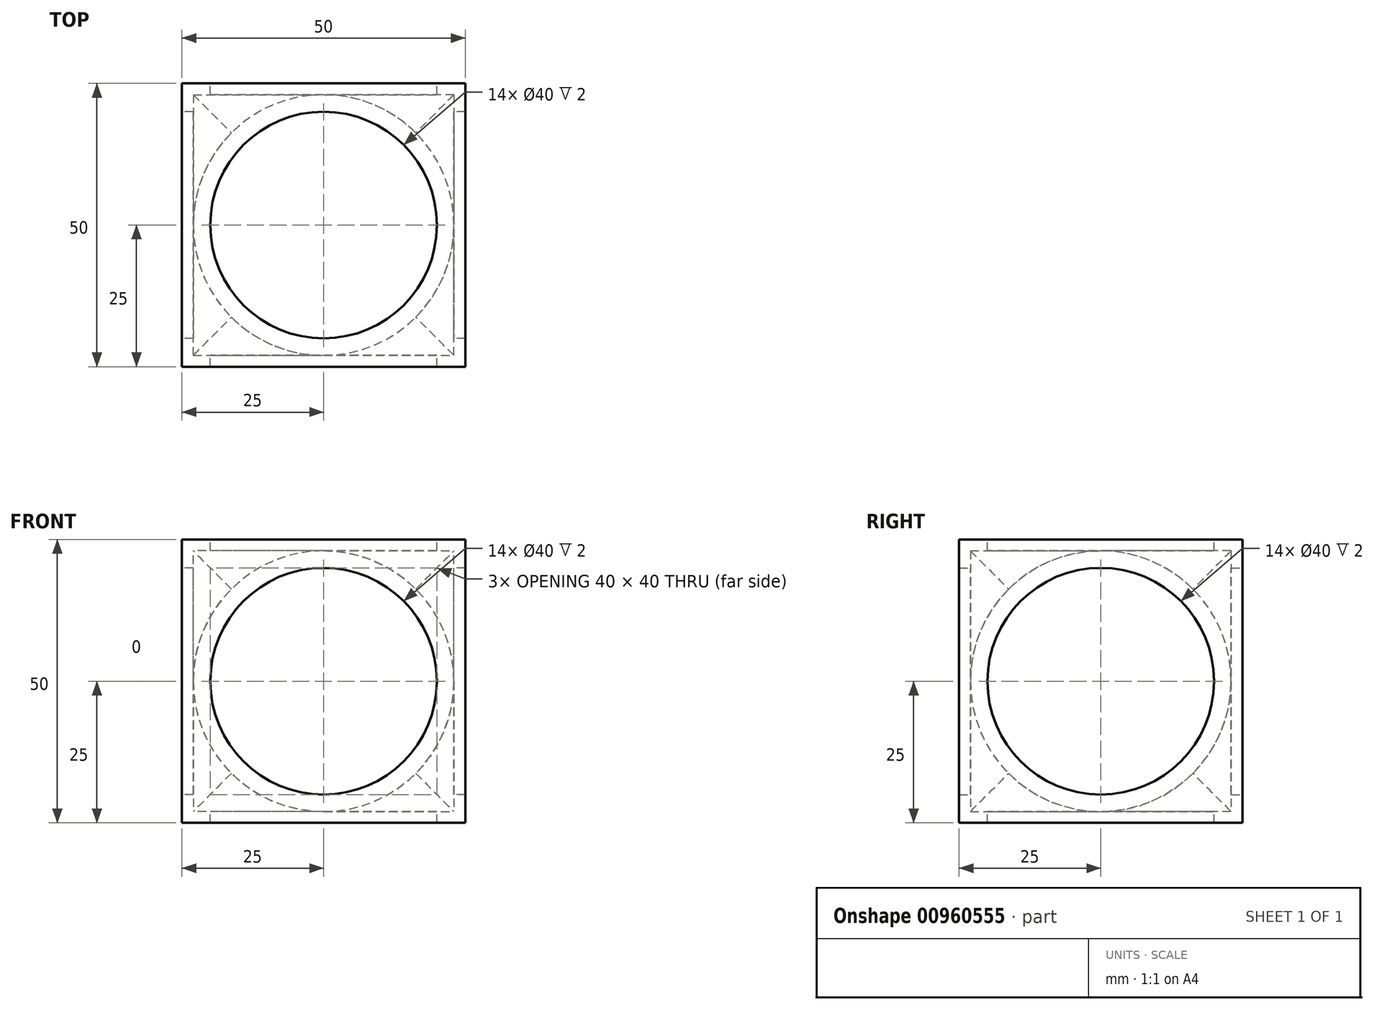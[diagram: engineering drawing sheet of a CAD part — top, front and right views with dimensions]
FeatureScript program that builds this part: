
annotation { "Feature Type Name" : "Feature", "Feature Type Description" : "" }
export const myFeature = defineFeature(function(context is Context, id is Id, definition is map)
    precondition{}
    {
        {
            var Q0;
            Q0=qCreatedBy(makeId("Top.planeOp"),FACE);
            var sketch = newSketch(context, id + "F0", { "sketchPlane" : qUnion([Q0])});
            skLineSegment(sketch, "E0.bottom", {"start": v(25, 25) * mm, "end": v(-25, 25) * mm});
            skLineSegment(sketch, "E0.top", {"start": v(25, -25) * mm, "end": v(-25, -25) * mm});
            skLineSegment(sketch, "E0.left", {"start": v(25, 25) * mm, "end": v(25, -25) * mm});
            skLineSegment(sketch, "E0.right", {"start": v(-25, 25) * mm, "end": v(-25, -25) * mm});
            skPoint(sketch, "E0.middle", {"position": v(0, 0) * mm});
            skSolve(sketch);
        }
        {
            var Q0;
            Q0 = qSketchRegion(id + "F0", true);
            extrude(context, id + "F1", {"entities" : qUnion([Q0]), "endBound" : BoundingType.SYMMETRIC, "depth" : 50 * mm, "offsetDistance" : 25 * mm});
        }
        {
            var Q0;
            Q0=makeQuery(id+"F1.opExtrude","CAP_FACE",FACE,{"disambiguationData":[OSD([sQuery(id+"F0.wireOp",EDGE,"E0.bottom"),sQuery(id+"F0.wireOp",EDGE,"E0.top"),sQuery(id+"F0.wireOp",EDGE,"E0.left"),sQuery(id+"F0.wireOp",EDGE,"E0.right")])],"isStart":false});
            var sketch = newSketch(context, id + "F2", { "sketchPlane" : qUnion([Q0])});
            skCircle(sketch, "E1", {"center": v(0, 0) * mm, "radius": 20 * mm});
            skSolve(sketch);
        }
        {
            var Q0;
            Q0 = qSketchRegion(id + "F2", true);
            extrude(context, id + "F3", {"entities" : qUnion([Q0]), "operationType" : NewBodyOperationType.REMOVE, "endBound" : BoundingType.THROUGH_ALL, "oppositeDirection" : true, "depth" : 25 * mm, "offsetDistance" : 25 * mm});
        }
        {
            var Q0;
            Q0=makeQuery(id+"F1.opExtrude","SWEPT_FACE",FACE,{"disambiguationData":[OSD([sQuery(id+"F0.wireOp",EDGE,"E0.bottom")])]});
            var sketch = newSketch(context, id + "F4", { "sketchPlane" : qUnion([Q0])});
            skCircle(sketch, "E2", {"center": v(0, 0) * mm, "radius": 20 * mm});
            skSolve(sketch);
        }
        {
            var Q0;
            Q0 = qSketchRegion(id + "F4", true);
            extrude(context, id + "F5", {"entities" : qUnion([Q0]), "operationType" : NewBodyOperationType.REMOVE, "endBound" : BoundingType.THROUGH_ALL, "oppositeDirection" : true, "depth" : 25 * mm, "offsetDistance" : 25 * mm});
        }
        {
            var Q0;
            Q0=makeQuery(id+"F1.opExtrude","SWEPT_FACE",FACE,{"disambiguationData":[OSD([sQuery(id+"F0.wireOp",EDGE,"E0.right")])]});
            var sketch = newSketch(context, id + "F6", { "sketchPlane" : qUnion([Q0])});
            skCircle(sketch, "E3", {"center": v(0, 0) * mm, "radius": 20 * mm});
            skSolve(sketch);
        }
        {
            var Q0;
            Q0 = qSketchRegion(id + "F6", true);
            extrude(context, id + "F7", {"entities" : qUnion([Q0]), "operationType" : NewBodyOperationType.REMOVE, "endBound" : BoundingType.THROUGH_ALL, "oppositeDirection" : true, "depth" : 25 * mm, "offsetDistance" : 25 * mm});
        }
        {
            var Q0;
            Q0=qCreatedBy(makeId("Top.planeOp"),FACE);
            var sketch = newSketch(context, id + "F8", { "sketchPlane" : qUnion([Q0])});
            skCircle(sketch, "E4", {"center": v(0, 0) * mm, "radius": 23 * mm});
            skSolve(sketch);
        }
        {
            var Q0;
            Q0 = qSketchRegion(id + "F8", true);
            extrude(context, id + "F9", {"entities" : qUnion([Q0]), "operationType" : NewBodyOperationType.REMOVE, "endBound" : BoundingType.SYMMETRIC, "oppositeDirection" : true, "depth" : 46 * mm, "offsetDistance" : 25 * mm});
        }
        {
            var Q0;
            Q0=qCreatedBy(makeId("Right.planeOp"),FACE);
            var sketch = newSketch(context, id + "F10", { "sketchPlane" : qUnion([Q0])});
            skCircle(sketch, "E5", {"center": v(0, 0) * mm, "radius": 23 * mm});
            skSolve(sketch);
        }
        {
            var Q0;
            Q0 = qSketchRegion(id + "F10", true);
            extrude(context, id + "F11", {"entities" : qUnion([Q0]), "operationType" : NewBodyOperationType.REMOVE, "endBound" : BoundingType.SYMMETRIC, "oppositeDirection" : true, "depth" : 46 * mm, "offsetDistance" : 25 * mm});
        }
        {
            var Q0;
            Q0=qCreatedBy(makeId("Front.planeOp"),FACE);
            var sketch = newSketch(context, id + "F12", { "sketchPlane" : qUnion([Q0])});
            skCircle(sketch, "E6", {"center": v(0, 0) * mm, "radius": 23 * mm});
            skSolve(sketch);
        }
        {
            var Q0;
            Q0 = qSketchRegion(id + "F12", true);
            extrude(context, id + "F13", {"entities" : qUnion([Q0]), "operationType" : NewBodyOperationType.REMOVE, "endBound" : BoundingType.SYMMETRIC, "oppositeDirection" : true, "depth" : 46 * mm, "offsetDistance" : 25 * mm});
        }
    });
